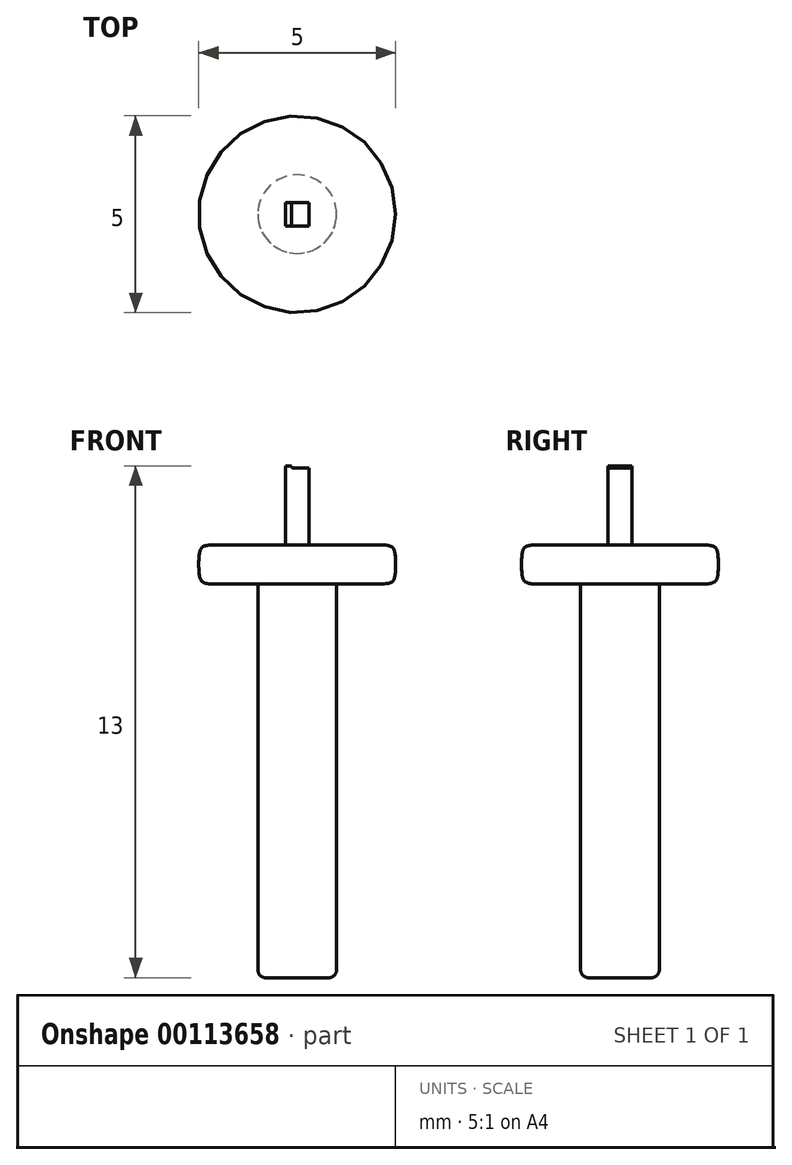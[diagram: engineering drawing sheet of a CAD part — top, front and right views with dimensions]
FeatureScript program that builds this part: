
annotation { "Feature Type Name" : "Feature", "Feature Type Description" : "" }
export const myFeature = defineFeature(function(context is Context, id is Id, definition is map)
    precondition{}
    {
        {
            var Q0;
            Q0=qCreatedBy(makeId("Top.planeOp"),FACE);
            var sketch = newSketch(context, id + "F0", { "sketchPlane" : qUnion([Q0])});
            skLineSegment(sketch, "E0.bottom", {"start": v(0.3, -0.3) * mm, "end": v(-0.3, -0.3) * mm});
            skLineSegment(sketch, "E0.top", {"start": v(0.3, 0.3) * mm, "end": v(-0.3, 0.3) * mm});
            skLineSegment(sketch, "E0.left", {"start": v(0.3, -0.3) * mm, "end": v(0.3, 0.3) * mm});
            skLineSegment(sketch, "E0.right", {"start": v(-0.3, -0.3) * mm, "end": v(-0.3, 0.3) * mm});
            skPoint(sketch, "E0.middle", {"position": v(0, 0) * mm});
            skSolve(sketch);
        }
        {
            var Q0;
            Q0=makeQuery(id+"F0.imprint","IMPRINT",FACE,{"disambiguationData":[TD([[makeQuery(id+"F0.imprint","IMPRINT",EDGE,{"derivedFrom":sQuery(id+"F0.wireOp",EDGE,"E0.bottom")}),-1.0]])]});
            extrude(context, id + "F1", {"entities" : qUnion([Q0]), "depth" : 2 * mm});
        }
        {
            var Q0;
            Q0=makeQuery(id+"F1.opExtrude","SWEPT_FACE",FACE,{"disambiguationData":[OSD([sQuery(id+"F0.wireOp",EDGE,"E0.bottom")])]});
            var sketch = newSketch(context, id + "F2", { "sketchPlane" : qUnion([Q0])});
            skLineSegment(sketch, "E1", {"start": v(0.3, 1.95) * mm, "end": v(-0.1, 1.95) * mm});
            skArc(sketch, "E2", {"start": v(-0.1, 1.95) * mm, "mid": v(-0.14, 1.96) * mm, "end": v(-0.15, 2) * mm});
            skSolve(sketch);
        }
        {
            var Q0;
            {var subQ0=sQuery(id+"F2.wireOp",EDGE,"E1");Q0=makeQuery(id+"F2.imprint","IMPRINT",FACE,{"disambiguationData":[TD([[makeQuery(id+"F2.imprint","IMPRINT",EDGE,{"derivedFrom":subQ0}),-1.0]])]});}
            extrude(context, id + "F3", {"entities" : qUnion([Q0]), "operationType" : NewBodyOperationType.REMOVE, "endBound" : BoundingType.UP_TO_NEXT, "oppositeDirection" : true, "depth" : 25 * mm});
        }
        {
            var Q0;
            Q0=qCreatedBy(makeId("Top.planeOp"),FACE);
            var sketch = newSketch(context, id + "F4", { "sketchPlane" : qUnion([Q0])});
            skCircle(sketch, "E3", {"center": v(0, 0) * mm, "radius": 2.5 * mm});
            skSolve(sketch);
        }
        {
            var Q0;
            Q0=makeQuery(id+"F4.imprint","IMPRINT",FACE,{"disambiguationData":[TD([[makeQuery(id+"F4.imprint","IMPRINT",EDGE,{"derivedFrom":sQuery(id+"F4.wireOp",EDGE,"E3")}),1.0]])]});
            extrude(context, id + "F5", {"entities" : qUnion([Q0]), "oppositeDirection" : true, "depth" : 1 * mm});
        }
        {
            var Q0;
            Q0=makeQuery(id+"F5.opExtrude","CAP_EDGE",EDGE,{"disambiguationData":[OSD([sQuery(id+"F4.wireOp",EDGE,"E3")])],"isStart":true});
            var Q1;
            Q1=makeQuery(id+"F5.opExtrude","CAP_EDGE",EDGE,{"disambiguationData":[OSD([sQuery(id+"F4.wireOp",EDGE,"E3")])],"isStart":false});
            fillet(context, id + "F6", {"entities" : qUnion([Q0, Q1]), "radius" : 0.5 * mm, "tangentPropagation" : true, "rho" : 0.7, "crossSection" : FilletCrossSection.CONIC, "allowEdgeOverflow" : false});
        }
        {
            var Q0;
            Q0=makeQuery(id+"F5.opExtrude","CAP_FACE",FACE,{"disambiguationData":[OSD([sQuery(id+"F4.wireOp",EDGE,"E3")])],"isStart":false});
            var sketch = newSketch(context, id + "F7", { "sketchPlane" : qUnion([Q0])});
            skCircle(sketch, "E4", {"center": v(0, 0) * mm, "radius": 1 * mm});
            skSolve(sketch);
        }
        {
            var Q0;
            Q0=makeQuery(id+"F7.imprint","IMPRINT",FACE,{"disambiguationData":[TD([[makeQuery(id+"F7.imprint","IMPRINT",EDGE,{"derivedFrom":sQuery(id+"F7.wireOp",EDGE,"E4")}),1.0]])]});
            extrude(context, id + "F8", {"entities" : qUnion([Q0]), "operationType" : NewBodyOperationType.ADD, "depth" : 10 * mm});
        }
        {
            var Q0;
            Q0=makeQuery(id+"F8.opExtrude","CAP_EDGE",EDGE,{"disambiguationData":[OSD([sQuery(id+"F7.wireOp",EDGE,"E4")])],"isStart":true});
            var Q1;
            Q1=makeQuery(id+"F8.opExtrude","CAP_EDGE",EDGE,{"disambiguationData":[OSD([sQuery(id+"F7.wireOp",EDGE,"E4")])],"isStart":false});
            fillet(context, id + "F9", {"entities" : qUnion([Q0, Q1]), "radius" : 0.2 * mm, "tangentPropagation" : true, "allowEdgeOverflow" : false});
        }
    });
